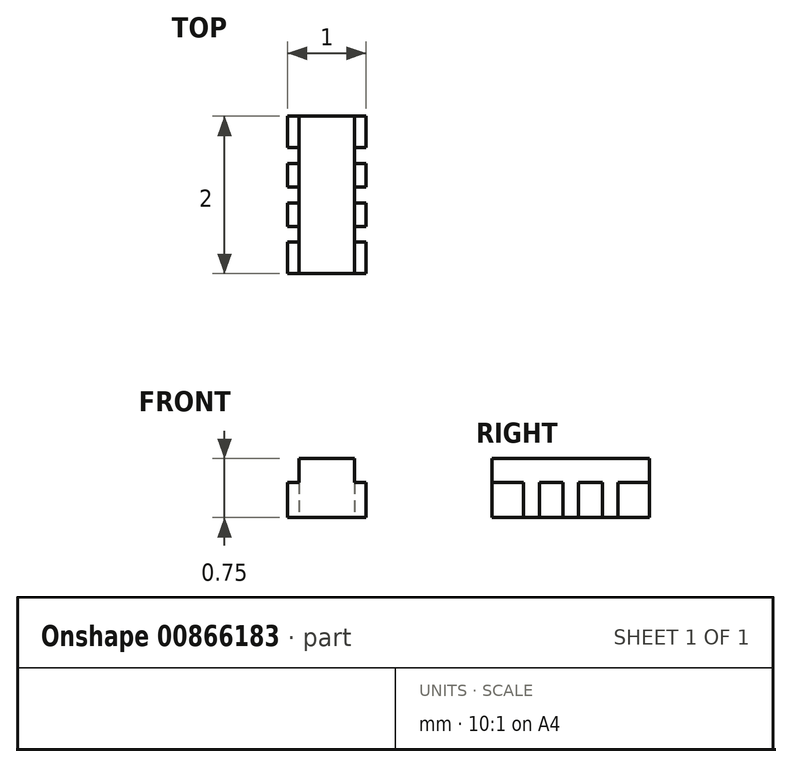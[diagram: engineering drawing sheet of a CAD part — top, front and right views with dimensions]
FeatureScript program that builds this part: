
annotation { "Feature Type Name" : "Feature", "Feature Type Description" : "" }
export const myFeature = defineFeature(function(context is Context, id is Id, definition is map)
    precondition{}
    {
        {
            var Q0;
            Q0=qCreatedBy(makeId("Top.planeOp"),FACE);
            var sketch = newSketch(context, id + "F0", { "sketchPlane" : qUnion([Q0])});
            skLineSegment(sketch, "E0.bottom", {"start": v(0.5, -1) * mm, "end": v(-0.5, -1) * mm});
            skLineSegment(sketch, "E0.top", {"start": v(0.5, 1) * mm, "end": v(-0.5, 1) * mm});
            skLineSegment(sketch, "E0.left", {"start": v(0.5, -1) * mm, "end": v(0.5, -0.6) * mm});
            skLineSegment(sketch, "E0.right", {"start": v(-0.5, -1) * mm, "end": v(-0.5, -0.6) * mm});
            skPoint(sketch, "E0.middle", {"position": v(0, 0) * mm});
            skLineSegment(sketch, "E1", {"start": v(-0.5, 1) * mm, "end": v(-0.5, 0.6) * mm});
            skLineSegment(sketch, "E2", {"start": v(-0.5, 0.6) * mm, "end": v(-0.35, 0.6) * mm});
            skLineSegment(sketch, "E3", {"start": v(-0.35, 0.6) * mm, "end": v(-0.35, 0.4) * mm});
            skLineSegment(sketch, "E4", {"start": v(-0.35, 0.4) * mm, "end": v(-0.5, 0.4) * mm});
            skLineSegment(sketch, "E5", {"start": v(-0.5, 0.4) * mm, "end": v(-0.5, 0.1) * mm});
            skLineSegment(sketch, "E6", {"start": v(-0.5, 0.1) * mm, "end": v(-0.35, 0.1) * mm});
            skLineSegment(sketch, "E7", {"start": v(-0.35, 0.1) * mm, "end": v(-0.35, -0.1) * mm});
            skLineSegment(sketch, "E8", {"start": v(-0.35, -0.1) * mm, "end": v(-0.5, -0.1) * mm});
            skLineSegment(sketch, "E9", {"start": v(-0.5, -0.1) * mm, "end": v(-0.5, -0.4) * mm});
            skLineSegment(sketch, "E10", {"start": v(-0.5, -0.4) * mm, "end": v(-0.35, -0.4) * mm});
            skLineSegment(sketch, "E11", {"start": v(-0.35, -0.4) * mm, "end": v(-0.35, -0.6) * mm});
            skLineSegment(sketch, "E12", {"start": v(-0.35, -0.6) * mm, "end": v(-0.5, -0.6) * mm});
            skLineSegment(sketch, "E13", {"start": v(-0.5, -0.6) * mm, "end": v(-0.5, -1) * mm});
            skLineSegment(sketch, "E14.trimOffspring", {"start": v(-0.5, 0.6) * mm, "end": v(-0.5, 1) * mm});
            skLineSegment(sketch, "E15.trimOffspring", {"start": v(-0.5, 0.1) * mm, "end": v(-0.5, 0.4) * mm});
            skLineSegment(sketch, "E16.trimOffspring", {"start": v(-0.5, -0.4) * mm, "end": v(-0.5, -0.1) * mm});
            skLineSegment(sketch, "E17", {"start": v(0.5, 1) * mm, "end": v(0.5, 0.6) * mm});
            skLineSegment(sketch, "E18", {"start": v(0.5, 0.6) * mm, "end": v(0.35, 0.6) * mm});
            skLineSegment(sketch, "E19", {"start": v(0.35, 0.6) * mm, "end": v(0.35, 0.4) * mm});
            skLineSegment(sketch, "E20", {"start": v(0.35, 0.4) * mm, "end": v(0.5, 0.4) * mm});
            skLineSegment(sketch, "E21", {"start": v(0.5, 0.4) * mm, "end": v(0.5, 0.1) * mm});
            skLineSegment(sketch, "E22", {"start": v(0.5, 0.1) * mm, "end": v(0.35, 0.1) * mm});
            skLineSegment(sketch, "E23", {"start": v(0.35, 0.1) * mm, "end": v(0.35, -0.1) * mm});
            skLineSegment(sketch, "E24", {"start": v(0.35, -0.1) * mm, "end": v(0.5, -0.1) * mm});
            skLineSegment(sketch, "E25", {"start": v(0.5, -0.1) * mm, "end": v(0.5, -0.4) * mm});
            skLineSegment(sketch, "E26", {"start": v(0.5, -0.4) * mm, "end": v(0.35, -0.4) * mm});
            skLineSegment(sketch, "E27", {"start": v(0.35, -0.4) * mm, "end": v(0.35, -0.6) * mm});
            skLineSegment(sketch, "E28", {"start": v(0.35, -0.6) * mm, "end": v(0.5, -0.6) * mm});
            skLineSegment(sketch, "E29", {"start": v(0.5, -0.6) * mm, "end": v(0.5, -1) * mm});
            skLineSegment(sketch, "E30.trimOffspring", {"start": v(0.5, -0.4) * mm, "end": v(0.5, -0.1) * mm});
            skLineSegment(sketch, "E31.trimOffspring", {"start": v(0.5, 0.1) * mm, "end": v(0.5, 0.4) * mm});
            skLineSegment(sketch, "E32.trimOffspring", {"start": v(0.5, 0.6) * mm, "end": v(0.5, 1) * mm});
            skSolve(sketch);
        }
        {
            var Q0;
            Q0=makeQuery(id+"F0.imprint","IMPRINT",FACE,{"disambiguationData":[TD([[makeQuery(id+"F0.imprint","IMPRINT",EDGE,{"derivedFrom":sQuery(id+"F0.wireOp",EDGE,"E0.bottom")}),-1.0]])]});
            extrude(context, id + "F1", {"entities" : qUnion([Q0]), "depth" : .45 * mm, "offsetDistance" : 25 * mm});
        }
        {
            var Q0;
            Q0=makeQuery(id+"F1.opExtrude","CAP_FACE",FACE,{"disambiguationData":[OSD([sQuery(id+"F0.wireOp",EDGE,"E0.bottom"),sQuery(id+"F0.wireOp",EDGE,"E0.top"),sQuery(id+"F0.wireOp",EDGE,"E2"),sQuery(id+"F0.wireOp",EDGE,"E3"),sQuery(id+"F0.wireOp",EDGE,"E4"),sQuery(id+"F0.wireOp",EDGE,"E6"),sQuery(id+"F0.wireOp",EDGE,"E7"),sQuery(id+"F0.wireOp",EDGE,"E8"),sQuery(id+"F0.wireOp",EDGE,"E10"),sQuery(id+"F0.wireOp",EDGE,"E11"),sQuery(id+"F0.wireOp",EDGE,"E12"),sQuery(id+"F0.wireOp",EDGE,"E13"),sQuery(id+"F0.wireOp",EDGE,"E14.trimOffspring"),sQuery(id+"F0.wireOp",EDGE,"E15.trimOffspring"),sQuery(id+"F0.wireOp",EDGE,"E16.trimOffspring"),sQuery(id+"F0.wireOp",EDGE,"E18"),sQuery(id+"F0.wireOp",EDGE,"E19"),sQuery(id+"F0.wireOp",EDGE,"E20"),sQuery(id+"F0.wireOp",EDGE,"E22"),sQuery(id+"F0.wireOp",EDGE,"E23"),sQuery(id+"F0.wireOp",EDGE,"E24"),sQuery(id+"F0.wireOp",EDGE,"E26"),sQuery(id+"F0.wireOp",EDGE,"E27"),sQuery(id+"F0.wireOp",EDGE,"E28"),sQuery(id+"F0.wireOp",EDGE,"E29"),sQuery(id+"F0.wireOp",EDGE,"E30.trimOffspring"),sQuery(id+"F0.wireOp",EDGE,"E31.trimOffspring"),sQuery(id+"F0.wireOp",EDGE,"E32.trimOffspring")])],"isStart":false});
            var sketch = newSketch(context, id + "F2", { "sketchPlane" : qUnion([Q0])});
            skLineSegment(sketch, "E33.bottom", {"start": v(0.35, 1) * mm, "end": v(-0.35, 1) * mm});
            skLineSegment(sketch, "E33.top", {"start": v(0.35, -1) * mm, "end": v(-0.35, -1) * mm});
            skLineSegment(sketch, "E33.left", {"start": v(0.35, 1) * mm, "end": v(0.35, -1) * mm});
            skLineSegment(sketch, "E33.right", {"start": v(-0.35, 1) * mm, "end": v(-0.35, -1) * mm});
            skPoint(sketch, "E33.middle", {"position": v(0, 0) * mm});
            skSolve(sketch);
        }
        {
            var Q0;
            Q0 = qSketchRegion(id + "F2", true);
            extrude(context, id + "F3", {"entities" : qUnion([Q0]), "operationType" : NewBodyOperationType.ADD, "depth" : .3 * mm, "offsetDistance" : 25 * mm});
        }
    });
